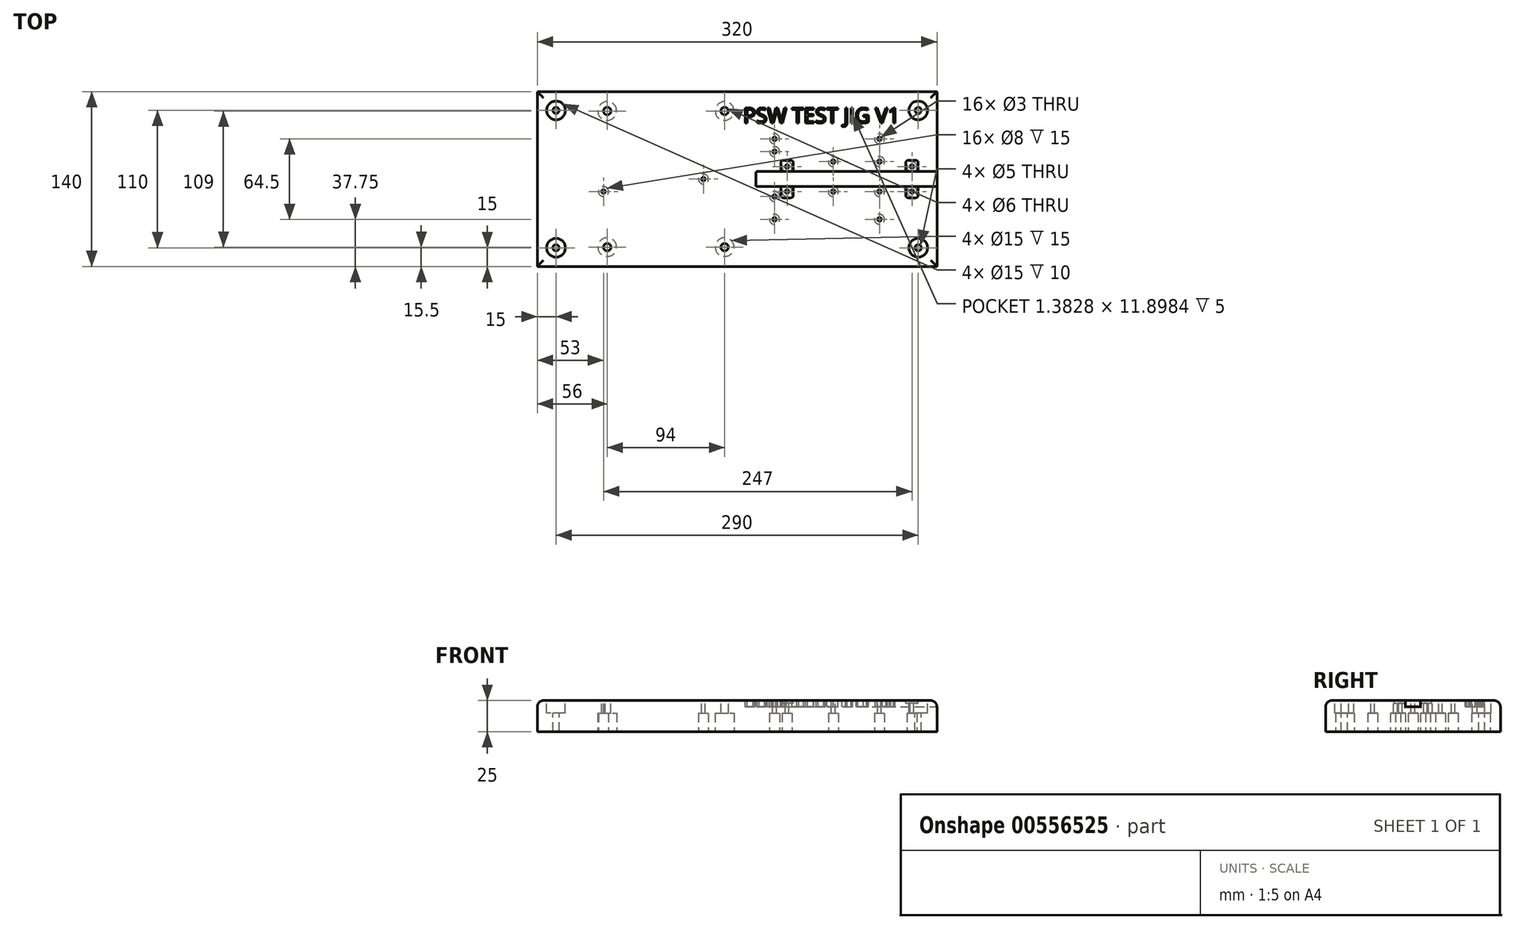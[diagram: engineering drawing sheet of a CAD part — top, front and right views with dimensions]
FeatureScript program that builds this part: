
annotation { "Feature Type Name" : "Feature", "Feature Type Description" : "" }
export const myFeature = defineFeature(function(context is Context, id is Id, definition is map)
    precondition{}
    {
        {
            var Q0;
            Q0=qCreatedBy(makeId("Top.planeOp"),FACE);
            var sketch = newSketch(context, id + "F0", { "sketchPlane" : qUnion([Q0])});
            skLineSegment(sketch, "E0.bottom", {"start": v(160, -70) * mm, "end": v(-160, -70) * mm});
            skLineSegment(sketch, "E0.top", {"start": v(160, 70) * mm, "end": v(-160, 70) * mm});
            skLineSegment(sketch, "E0.left", {"start": v(160, -70) * mm, "end": v(160, 70) * mm});
            skLineSegment(sketch, "E0.right", {"start": v(-160, -70) * mm, "end": v(-160, 70) * mm});
            skPoint(sketch, "E0.middle", {"position": v(0, 0) * mm});
            skSolve(sketch);
        }
        {
            var Q0;
            Q0 = qSketchRegion(id + "F0", true);
            extrude(context, id + "F1", {"entities" : qUnion([Q0]), "depth" : 25 * mm, "offsetDistance" : 25 * mm});
        }
        {
            var Q0;
            Q0=makeQuery(id+"F1.opExtrude","CAP_EDGE",EDGE,{"disambiguationData":[OSD([sQuery(id+"F0.wireOp",EDGE,"E0.right")])],"isStart":false});
            var Q1;
            Q1=makeQuery(id+"F1.opExtrude","CAP_EDGE",EDGE,{"disambiguationData":[OSD([sQuery(id+"F0.wireOp",EDGE,"E0.top")])],"isStart":false});
            var Q2;
            Q2=makeQuery(id+"F1.opExtrude","CAP_EDGE",EDGE,{"disambiguationData":[OSD([sQuery(id+"F0.wireOp",EDGE,"E0.left")])],"isStart":false});
            var Q3;
            Q3=makeQuery(id+"F1.opExtrude","CAP_EDGE",EDGE,{"disambiguationData":[OSD([sQuery(id+"F0.wireOp",EDGE,"E0.bottom")])],"isStart":false});
            fillet(context, id + "F2", {"entities" : qUnion([Q0, Q1, Q2, Q3]), "radius" : 5 * mm, "tangentPropagation" : true, "allowEdgeOverflow" : false});
        }
        {
            var Q0;
            Q0=makeQuery(id+"F1.opExtrude","CAP_FACE",FACE,{"disambiguationData":[OSD([sQuery(id+"F0.wireOp",EDGE,"E0.bottom"),sQuery(id+"F0.wireOp",EDGE,"E0.top"),sQuery(id+"F0.wireOp",EDGE,"E0.left"),sQuery(id+"F0.wireOp",EDGE,"E0.right")])],"isStart":false});
            var sketch = newSketch(context, id + "F3", { "sketchPlane" : qUnion([Q0])});
            skLineSegment(sketch, "E1", {"start": v(-346.3, 45) * mm, "end": v(340.15, 45) * mm, "construction": true});
            skText(sketch, "E2", { "text": "PSW TEST JIG V1", "fontName": "OpenSans-Regular.ttf"});
            const initialGuessF3  = {"E2": [0.005, 0.045, 1, 0, 0.012]};
            skSetInitialGuess(sketch, initialGuessF3);
            skSolve(sketch);
        }
        {
            var Q0;
            Q0 = qSketchRegion(id + "F3", true);
            extrude(context, id + "F4", {"entities" : qUnion([Q0]), "operationType" : NewBodyOperationType.REMOVE, "oppositeDirection" : true, "depth" : 5 * mm, "offsetDistance" : 25 * mm});
        }
        {
            var Q0;
            Q0=makeQuery(id+"F1.opExtrude","CAP_FACE",FACE,{"disambiguationData":[OSD([sQuery(id+"F0.wireOp",EDGE,"E0.bottom"),sQuery(id+"F0.wireOp",EDGE,"E0.top"),sQuery(id+"F0.wireOp",EDGE,"E0.left"),sQuery(id+"F0.wireOp",EDGE,"E0.right")])],"isStart":false});
            var sketch = newSketch(context, id + "F5", { "sketchPlane" : qUnion([Q0])});
            skCircle(sketch, "E3", {"center": v(-104, 54.5) * mm, "radius": 3 * mm});
            skLineSegment(sketch, "E4", {"start": v(-173, 0) * mm, "end": v(190.46, 0) * mm, "construction": true});
            skPoint(sketch, "E4.startSnap0", {"position": v(-155, 0) * mm});
            skCircle(sketch, "E5", {"center": v(-10, 54.5) * mm, "radius": 3 * mm});
            skLineSegment(sketch, "E6", {"start": v(0, 91.65) * mm, "end": v(0, -104.84) * mm, "construction": true});
            skCircle(sketch, "E7.MirrorC", {"center": v(-104, -54.5) * mm, "radius": 3 * mm});
            skCircle(sketch, "E8.MirrorC", {"center": v(-10, -54.5) * mm, "radius": 3 * mm});
            skCircle(sketch, "E9", {"center": v(-27, 0) * mm, "radius": 1.5 * mm});
            skCircle(sketch, "E10", {"center": v(-107, -10) * mm, "radius": 1.5 * mm});
            skSolve(sketch);
        }
        {
            var Q0;
            Q0 = qSketchRegion(id + "F5", true);
            extrude(context, id + "F6", {"entities" : qUnion([Q0]), "operationType" : NewBodyOperationType.REMOVE, "oppositeDirection" : true, "depth" : 25 * mm, "offsetDistance" : 25 * mm});
        }
        {
            var Q0;
            Q0=makeQuery(id+"F1.opExtrude","CAP_FACE",FACE,{"disambiguationData":[OSD([sQuery(id+"F0.wireOp",EDGE,"E0.bottom"),sQuery(id+"F0.wireOp",EDGE,"E0.top"),sQuery(id+"F0.wireOp",EDGE,"E0.left"),sQuery(id+"F0.wireOp",EDGE,"E0.right")])],"isStart":true});
            var sketch = newSketch(context, id + "F7", { "sketchPlane" : qUnion([Q0])});
            skCircle(sketch, "E11", {"center": v(-104, 54.5) * mm, "radius": 7.5 * mm});
            skCircle(sketch, "E12", {"center": v(-10, 54.5) * mm, "radius": 7.5 * mm});
            skCircle(sketch, "E13", {"center": v(-10, -54.5) * mm, "radius": 7.5 * mm});
            skCircle(sketch, "E14", {"center": v(-104, -54.5) * mm, "radius": 7.5 * mm});
            skCircle(sketch, "E15", {"center": v(-107, 10) * mm, "radius": 4 * mm});
            skCircle(sketch, "E16", {"center": v(-27, 0) * mm, "radius": 4 * mm});
            skSolve(sketch);
        }
        {
            var Q0;
            Q0 = qSketchRegion(id + "F7", true);
            extrude(context, id + "F8", {"entities" : qUnion([Q0]), "operationType" : NewBodyOperationType.REMOVE, "oppositeDirection" : true, "depth" : 15 * mm, "offsetDistance" : 25 * mm});
        }
        {
            var Q0;
            Q0=makeQuery(id+"F1.opExtrude","CAP_FACE",FACE,{"disambiguationData":[OSD([sQuery(id+"F0.wireOp",EDGE,"E0.bottom"),sQuery(id+"F0.wireOp",EDGE,"E0.top"),sQuery(id+"F0.wireOp",EDGE,"E0.left"),sQuery(id+"F0.wireOp",EDGE,"E0.right")])],"isStart":false});
            var sketch = newSketch(context, id + "F9", { "sketchPlane" : qUnion([Q0])});
            skLineSegment(sketch, "E17", {"start": v(-172.65, 0) * mm, "end": v(214.17, 0) * mm, "construction": true});
            skLineSegment(sketch, "E18", {"start": v(0, 95.62) * mm, "end": v(0, -102.66) * mm, "construction": true});
            skCircle(sketch, "E19", {"center": v(30, 32.25) * mm, "radius": 1.5 * mm});
            skCircle(sketch, "E20", {"center": v(114, 32.25) * mm, "radius": 1.5 * mm});
            skCircle(sketch, "E21.MirrorC", {"center": v(30, -32.25) * mm, "radius": 1.5 * mm});
            skCircle(sketch, "E22.MirrorC", {"center": v(114, -32.25) * mm, "radius": 1.5 * mm});
            skSolve(sketch);
        }
        {
            var Q0;
            Q0 = qSketchRegion(id + "F9", true);
            extrude(context, id + "F10", {"entities" : qUnion([Q0]), "operationType" : NewBodyOperationType.REMOVE, "oppositeDirection" : true, "depth" : 25 * mm, "offsetDistance" : 25 * mm});
        }
        {
            var Q0;
            Q0=makeQuery(id+"F1.opExtrude","CAP_FACE",FACE,{"disambiguationData":[OSD([sQuery(id+"F0.wireOp",EDGE,"E0.bottom"),sQuery(id+"F0.wireOp",EDGE,"E0.top"),sQuery(id+"F0.wireOp",EDGE,"E0.left"),sQuery(id+"F0.wireOp",EDGE,"E0.right")])],"isStart":true});
            var sketch = newSketch(context, id + "F11", { "sketchPlane" : qUnion([Q0])});
            skCircle(sketch, "E23", {"center": v(30, 32.25) * mm, "radius": 4 * mm});
            skCircle(sketch, "E24", {"center": v(114, 32.25) * mm, "radius": 4 * mm});
            skCircle(sketch, "E25", {"center": v(114, -32.25) * mm, "radius": 4 * mm});
            skCircle(sketch, "E26", {"center": v(30, -32.25) * mm, "radius": 4 * mm});
            skSolve(sketch);
        }
        {
            var Q0;
            Q0 = qSketchRegion(id + "F11", true);
            extrude(context, id + "F12", {"entities" : qUnion([Q0]), "operationType" : NewBodyOperationType.REMOVE, "oppositeDirection" : true, "depth" : 15 * mm, "offsetDistance" : 25 * mm});
        }
        {
            var Q0;
            Q0=makeQuery(id+"F1.opExtrude","CAP_FACE",FACE,{"disambiguationData":[OSD([sQuery(id+"F0.wireOp",EDGE,"E0.bottom"),sQuery(id+"F0.wireOp",EDGE,"E0.top"),sQuery(id+"F0.wireOp",EDGE,"E0.left"),sQuery(id+"F0.wireOp",EDGE,"E0.right")])],"isStart":false});
            var sketch = newSketch(context, id + "F13", { "sketchPlane" : qUnion([Q0])});
            skLineSegment(sketch, "E27", {"start": v(-174.59, 0) * mm, "end": v(211.52, 0) * mm, "construction": true});
            skLineSegment(sketch, "E28", {"start": v(0, 99.62) * mm, "end": v(0, -109.76) * mm, "construction": true});
            skCircle(sketch, "E29", {"center": v(-145, 55) * mm, "radius": 2.5 * mm});
            skCircle(sketch, "E30.MirrorC", {"center": v(-145, -55) * mm, "radius": 2.5 * mm});
            skLineSegment(sketch, "E31.MirrorCS", {"start": v(0, -99.62) * mm, "end": v(0, 109.76) * mm, "construction": true});
            skCircle(sketch, "E32.MirrorC", {"center": v(145, 55) * mm, "radius": 2.5 * mm});
            skCircle(sketch, "E33.MirrorC", {"center": v(145, -55) * mm, "radius": 2.5 * mm});
            skSolve(sketch);
        }
        {
            var Q0;
            Q0 = qSketchRegion(id + "F13", true);
            extrude(context, id + "F14", {"entities" : qUnion([Q0]), "operationType" : NewBodyOperationType.REMOVE, "oppositeDirection" : true, "depth" : 25 * mm, "offsetDistance" : 25 * mm});
        }
        {
            var Q0;
            Q0=makeQuery(id+"F1.opExtrude","CAP_FACE",FACE,{"disambiguationData":[OSD([sQuery(id+"F0.wireOp",EDGE,"E0.bottom"),sQuery(id+"F0.wireOp",EDGE,"E0.top"),sQuery(id+"F0.wireOp",EDGE,"E0.left"),sQuery(id+"F0.wireOp",EDGE,"E0.right")])],"isStart":false});
            var sketch = newSketch(context, id + "F15", { "sketchPlane" : qUnion([Q0])});
            skCircle(sketch, "E34", {"center": v(-145, 55) * mm, "radius": 7.5 * mm});
            skCircle(sketch, "E35", {"center": v(-145, -55) * mm, "radius": 7.5 * mm});
            skCircle(sketch, "E36", {"center": v(145, -55) * mm, "radius": 7.5 * mm});
            skCircle(sketch, "E37", {"center": v(145, 55) * mm, "radius": 7.5 * mm});
            skSolve(sketch);
        }
        {
            var Q0;
            Q0 = qSketchRegion(id + "F15", true);
            extrude(context, id + "F16", {"entities" : qUnion([Q0]), "operationType" : NewBodyOperationType.REMOVE, "oppositeDirection" : true, "depth" : 10 * mm, "offsetDistance" : 25 * mm});
        }
        {
            var Q0;
            {var subQ0=sQuery(id+"F0.wireOp",EDGE,"E0.right");var subQ1=sQuery(id+"F0.wireOp",EDGE,"E0.left");var subQ2=sQuery(id+"F0.wireOp",EDGE,"E0.top");var subQ3=sQuery(id+"F0.wireOp",EDGE,"E0.bottom");Q0=makeQuery(id+"F4.boolean.opBoolean","SPLIT",FACE,{"disambiguationData":[TD([makeQuery(id+"F2.opFillet","BLEND_FACE",FACE,{"disambiguationData":[OSD([subQ3])]})])],"derivedFrom":makeQuery(id+"F1.opExtrude","CAP_FACE",FACE,{"disambiguationData":[OSD([subQ3,subQ2,subQ1,subQ0])],"isStart":false})});}
            var sketch = newSketch(context, id + "F17", { "sketchPlane" : qUnion([Q0])});
            skLineSegment(sketch, "E38", {"start": v(-182.2, 0) * mm, "end": v(196.75, 0) * mm, "construction": true});
            skPoint(sketch, "E38.startSnap0", {"position": v(-155, 0) * mm});
            skCircle(sketch, "E39", {"center": v(114, 14) * mm, "radius": 1.5 * mm});
            skCircle(sketch, "E40", {"center": v(77, 14) * mm, "radius": 1.5 * mm});
            skCircle(sketch, "E41", {"center": v(30, 22) * mm, "radius": 1.5 * mm});
            skCircle(sketch, "E42", {"center": v(30, -14) * mm, "radius": 1.5 * mm});
            skCircle(sketch, "E43", {"center": v(77, -10) * mm, "radius": 1.5 * mm});
            skCircle(sketch, "E44", {"center": v(114, -10) * mm, "radius": 1.5 * mm});
            skLineSegment(sketch, "E45", {"start": v(30, 32.25) * mm, "end": v(30, -32.25) * mm, "construction": true});
            skSolve(sketch);
        }
        {
            var Q0;
            Q0 = qSketchRegion(id + "F17", true);
            extrude(context, id + "F18", {"entities" : qUnion([Q0]), "operationType" : NewBodyOperationType.REMOVE, "oppositeDirection" : true, "depth" : 25 * mm, "offsetDistance" : 25 * mm});
        }
        {
            var Q0;
            Q0=makeQuery(id+"F1.opExtrude","CAP_FACE",FACE,{"disambiguationData":[OSD([sQuery(id+"F0.wireOp",EDGE,"E0.bottom"),sQuery(id+"F0.wireOp",EDGE,"E0.top"),sQuery(id+"F0.wireOp",EDGE,"E0.left"),sQuery(id+"F0.wireOp",EDGE,"E0.right")])],"isStart":true});
            var sketch = newSketch(context, id + "F19", { "sketchPlane" : qUnion([Q0])});
            skCircle(sketch, "E46", {"center": v(30, 14) * mm, "radius": 4 * mm});
            skCircle(sketch, "E47", {"center": v(77, 10) * mm, "radius": 4 * mm});
            skCircle(sketch, "E48", {"center": v(114, 10) * mm, "radius": 4 * mm});
            skCircle(sketch, "E49", {"center": v(114, -14) * mm, "radius": 4 * mm});
            skCircle(sketch, "E50", {"center": v(77, -14) * mm, "radius": 4 * mm});
            skCircle(sketch, "E51", {"center": v(30, -22) * mm, "radius": 4 * mm});
            skSolve(sketch);
        }
        {
            var Q0;
            Q0 = qSketchRegion(id + "F19", true);
            extrude(context, id + "F20", {"entities" : qUnion([Q0]), "operationType" : NewBodyOperationType.REMOVE, "oppositeDirection" : true, "depth" : 15 * mm, "offsetDistance" : 25 * mm});
        }
        {
            var Q0;
            {var subQ0=sQuery(id+"F0.wireOp",EDGE,"E0.right");var subQ1=sQuery(id+"F0.wireOp",EDGE,"E0.left");var subQ2=sQuery(id+"F0.wireOp",EDGE,"E0.top");var subQ3=sQuery(id+"F0.wireOp",EDGE,"E0.bottom");Q0=makeQuery(id+"F4.boolean.opBoolean","SPLIT",FACE,{"disambiguationData":[TD([makeQuery(id+"F2.opFillet","BLEND_FACE",FACE,{"disambiguationData":[OSD([subQ3])]})])],"derivedFrom":makeQuery(id+"F1.opExtrude","CAP_FACE",FACE,{"disambiguationData":[OSD([subQ3,subQ2,subQ1,subQ0])],"isStart":false})});}
            var sketch = newSketch(context, id + "F21", { "sketchPlane" : qUnion([Q0])});
            skLineSegment(sketch, "E52.bottom", {"start": v(15, -6) * mm, "end": v(160, -6) * mm});
            skLineSegment(sketch, "E52.top", {"start": v(15, 6) * mm, "end": v(160, 6) * mm});
            skLineSegment(sketch, "E52.left", {"start": v(15, -6) * mm, "end": v(15, 6) * mm});
            skLineSegment(sketch, "E52.right", {"start": v(160, -6) * mm, "end": v(160, 6) * mm});
            skSolve(sketch);
        }
        {
            var Q0;
            Q0 = qSketchRegion(id + "F21", true);
            extrude(context, id + "F22", {"entities" : qUnion([Q0]), "operationType" : NewBodyOperationType.REMOVE, "oppositeDirection" : true, "depth" : 5 * mm, "offsetDistance" : 25 * mm});
        }
        {
            var Q0;
            Q0=makeQuery(id+"F22.boolean.opBoolean","COPY",EDGE,{"derivedFrom":makeQuery(id+"F22.opExtrude","CAP_EDGE",EDGE,{"disambiguationData":[OSD([sQuery(id+"F21.wireOp",EDGE,"E52.left")])],"isStart":true})});
            var Q1;
            Q1=makeQuery(id+"F22.boolean.opBoolean","COPY",EDGE,{"derivedFrom":makeQuery(id+"F22.opExtrude","SWEPT_EDGE",EDGE,{"disambiguationData":[OSD([sQuery(id+"F21.wireOp",EDGE,"E52.top"),sQuery(id+"F21.wireOp",EDGE,"E52.left")])]})});
            var Q2;
            Q2=makeQuery(id+"F22.boolean.opBoolean","COPY",EDGE,{"derivedFrom":makeQuery(id+"F22.opExtrude","SWEPT_EDGE",EDGE,{"disambiguationData":[OSD([sQuery(id+"F21.wireOp",EDGE,"E52.bottom"),sQuery(id+"F21.wireOp",EDGE,"E52.left")])]})});
            var Q3;
            Q3=makeQuery(id+"F22.boolean.opBoolean","COPY",EDGE,{"derivedFrom":makeQuery(id+"F22.opExtrude","CAP_EDGE",EDGE,{"disambiguationData":[OSD([sQuery(id+"F21.wireOp",EDGE,"E52.right")])],"isStart":false})});
            var Q4;
            {var subQ0=sQuery(id+"F0.wireOp",EDGE,"E0.left");Q4=makeQuery(id+"F22.boolean.opBoolean","MERGE",EDGE,{"derivedFrom":[makeQuery(id+"F2.opFillet","BLEND_EDGE",EDGE,{"blendedFrom":[makeQuery(id+"F1.opExtrude","CAP_EDGE",EDGE,{"disambiguationData":[OSD([subQ0])],"isStart":false}),makeQuery(id+"F1.opExtrude","SWEPT_FACE",FACE,{"disambiguationData":[OSD([subQ0])]})],"blendedInto":[makeQuery(id+"F1.opExtrude","SWEPT_FACE",FACE,{"disambiguationData":[OSD([subQ0])]})]}),makeQuery(id+"F22.opExtrude","CAP_EDGE",EDGE,{"disambiguationData":[OSD([sQuery(id+"F21.wireOp",EDGE,"E52.right")])],"isStart":false})]});}
            fillet(context, id + "F23", {"entities" : qUnion([Q0, Q1, Q2, Q3, Q4]), "radius" : 1 * mm, "tangentPropagation" : true, "allowEdgeOverflow" : false});
        }
        {
            var Q0;
            {var subQ0=sQuery(id+"F0.wireOp",EDGE,"E0.right");var subQ1=sQuery(id+"F0.wireOp",EDGE,"E0.left");var subQ2=sQuery(id+"F0.wireOp",EDGE,"E0.top");var subQ3=sQuery(id+"F0.wireOp",EDGE,"E0.bottom");Q0=makeQuery(id+"F4.boolean.opBoolean","SPLIT",FACE,{"disambiguationData":[TD([makeQuery(id+"F2.opFillet","BLEND_FACE",FACE,{"disambiguationData":[OSD([subQ3])]})])],"derivedFrom":makeQuery(id+"F1.opExtrude","CAP_FACE",FACE,{"disambiguationData":[OSD([subQ3,subQ2,subQ1,subQ0])],"isStart":false})});}
            var sketch = newSketch(context, id + "F24", { "sketchPlane" : qUnion([Q0])});
            skLineSegment(sketch, "E53", {"start": v(-16.3, 0) * mm, "end": v(165.04, 0) * mm, "construction": true});
            skLineSegment(sketch, "E54.bottom", {"start": v(45, -15) * mm, "end": v(35, -15) * mm});
            skLineSegment(sketch, "E54.top", {"start": v(45, 15) * mm, "end": v(35, 15) * mm});
            skLineSegment(sketch, "E54.left", {"start": v(45, -15) * mm, "end": v(45, 15) * mm});
            skLineSegment(sketch, "E54.right", {"start": v(35, -15) * mm, "end": v(35, 15) * mm});
            skPoint(sketch, "E54.middle", {"position": v(40, 0) * mm});
            skLineSegment(sketch, "E55.bottom", {"start": v(145, -15) * mm, "end": v(135, -15) * mm});
            skLineSegment(sketch, "E55.top", {"start": v(145, 15) * mm, "end": v(135, 15) * mm});
            skLineSegment(sketch, "E55.left", {"start": v(145, -15) * mm, "end": v(145, 15) * mm});
            skLineSegment(sketch, "E55.right", {"start": v(135, -15) * mm, "end": v(135, 15) * mm});
            skPoint(sketch, "E55.middle", {"position": v(140, 0) * mm});
            skLineSegment(sketch, "E56", {"start": v(0, 78.47) * mm, "end": v(0, -93.79) * mm, "construction": true});
            skSolve(sketch);
        }
        {
            var Q0;
            Q0 = qSketchRegion(id + "F24", true);
            extrude(context, id + "F25", {"entities" : qUnion([Q0]), "operationType" : NewBodyOperationType.REMOVE, "oppositeDirection" : true, "depth" : 2 * mm, "offsetDistance" : 25 * mm});
        }
        {
            var Q0;
            Q0=makeQuery(id+"F25.boolean.opBoolean","COPY",EDGE,{"derivedFrom":makeQuery(id+"F25.opExtrude","SWEPT_EDGE",EDGE,{"disambiguationData":[OSD([sQuery(id+"F24.wireOp",EDGE,"E54.top"),sQuery(id+"F24.wireOp",EDGE,"E54.right")])]})});
            var Q1;
            Q1=makeQuery(id+"F25.boolean.opBoolean","COPY",EDGE,{"derivedFrom":makeQuery(id+"F25.opExtrude","SWEPT_EDGE",EDGE,{"disambiguationData":[OSD([sQuery(id+"F24.wireOp",EDGE,"E54.top"),sQuery(id+"F24.wireOp",EDGE,"E54.left")])]})});
            var Q2;
            Q2=makeQuery(id+"F25.boolean.opBoolean","COPY",EDGE,{"derivedFrom":makeQuery(id+"F25.opExtrude","SWEPT_EDGE",EDGE,{"disambiguationData":[OSD([sQuery(id+"F24.wireOp",EDGE,"E54.bottom"),sQuery(id+"F24.wireOp",EDGE,"E54.right")])]})});
            var Q3;
            Q3=makeQuery(id+"F25.boolean.opBoolean","COPY",EDGE,{"derivedFrom":makeQuery(id+"F25.opExtrude","SWEPT_EDGE",EDGE,{"disambiguationData":[OSD([sQuery(id+"F24.wireOp",EDGE,"E54.bottom"),sQuery(id+"F24.wireOp",EDGE,"E54.left")])]})});
            var Q4;
            Q4=makeQuery(id+"F25.boolean.opBoolean","COPY",EDGE,{"derivedFrom":makeQuery(id+"F25.opExtrude","SWEPT_EDGE",EDGE,{"disambiguationData":[OSD([sQuery(id+"F24.wireOp",EDGE,"E55.top"),sQuery(id+"F24.wireOp",EDGE,"E55.right")])]})});
            var Q5;
            Q5=makeQuery(id+"F25.boolean.opBoolean","COPY",EDGE,{"derivedFrom":makeQuery(id+"F25.opExtrude","SWEPT_EDGE",EDGE,{"disambiguationData":[OSD([sQuery(id+"F24.wireOp",EDGE,"E55.top"),sQuery(id+"F24.wireOp",EDGE,"E55.left")])]})});
            var Q6;
            Q6=makeQuery(id+"F25.boolean.opBoolean","COPY",EDGE,{"derivedFrom":makeQuery(id+"F25.opExtrude","SWEPT_EDGE",EDGE,{"disambiguationData":[OSD([sQuery(id+"F24.wireOp",EDGE,"E55.bottom"),sQuery(id+"F24.wireOp",EDGE,"E55.right")])]})});
            var Q7;
            Q7=makeQuery(id+"F25.boolean.opBoolean","COPY",EDGE,{"derivedFrom":makeQuery(id+"F25.opExtrude","SWEPT_EDGE",EDGE,{"disambiguationData":[OSD([sQuery(id+"F24.wireOp",EDGE,"E55.bottom"),sQuery(id+"F24.wireOp",EDGE,"E55.left")])]})});
            fillet(context, id + "F26", {"entities" : qUnion([Q0, Q1, Q2, Q3, Q4, Q5, Q6, Q7]), "radius" : 2 * mm, "tangentPropagation" : true, "allowEdgeOverflow" : false});
        }
        {
            var Q0;
            {var subQ0=sQuery(id+"F0.wireOp",EDGE,"E0.right");var subQ1=sQuery(id+"F0.wireOp",EDGE,"E0.left");var subQ2=sQuery(id+"F0.wireOp",EDGE,"E0.top");var subQ3=sQuery(id+"F0.wireOp",EDGE,"E0.bottom");Q0=makeQuery(id+"F4.boolean.opBoolean","SPLIT",FACE,{"disambiguationData":[TD([makeQuery(id+"F2.opFillet","BLEND_FACE",FACE,{"disambiguationData":[OSD([subQ3])]})])],"derivedFrom":makeQuery(id+"F1.opExtrude","CAP_FACE",FACE,{"disambiguationData":[OSD([subQ3,subQ2,subQ1,subQ0])],"isStart":false})});}
            var sketch = newSketch(context, id + "F27", { "sketchPlane" : qUnion([Q0])});
            skLineSegment(sketch, "E57", {"start": v(0, 0) * mm, "end": v(193.75, 0) * mm, "construction": true});
            skLineSegment(sketch, "E58", {"start": v(0, 81.91) * mm, "end": v(0, -80.5) * mm, "construction": true});
            skLineSegment(sketch, "E59", {"start": v(40, 15) * mm, "end": v(40, -15) * mm, "construction": true});
            skLineSegment(sketch, "E60", {"start": v(140, 15) * mm, "end": v(140, -15) * mm, "construction": true});
            skLineSegment(sketch, "E61", {"start": v(40, 10) * mm, "end": v(140, 10) * mm, "construction": true});
            skLineSegment(sketch, "E62", {"start": v(40, -10) * mm, "end": v(140, -10) * mm, "construction": true});
            skCircle(sketch, "E63", {"center": v(40, 10) * mm, "radius": 1.5 * mm});
            skCircle(sketch, "E64", {"center": v(140, 10) * mm, "radius": 1.5 * mm});
            skCircle(sketch, "E65", {"center": v(40, -10) * mm, "radius": 1.5 * mm});
            skCircle(sketch, "E66", {"center": v(140, -10) * mm, "radius": 1.5 * mm});
            skSolve(sketch);
        }
        {
            var Q0;
            Q0 = qSketchRegion(id + "F27", true);
            extrude(context, id + "F28", {"entities" : qUnion([Q0]), "operationType" : NewBodyOperationType.REMOVE, "oppositeDirection" : true, "depth" : 25 * mm, "offsetDistance" : 25 * mm});
        }
        {
            var Q0;
            Q0=makeQuery(id+"F1.opExtrude","CAP_FACE",FACE,{"disambiguationData":[OSD([sQuery(id+"F0.wireOp",EDGE,"E0.bottom"),sQuery(id+"F0.wireOp",EDGE,"E0.top"),sQuery(id+"F0.wireOp",EDGE,"E0.left"),sQuery(id+"F0.wireOp",EDGE,"E0.right")])],"isStart":true});
            var sketch = newSketch(context, id + "F29", { "sketchPlane" : qUnion([Q0])});
            skCircle(sketch, "E67", {"center": v(40, -10) * mm, "radius": 4 * mm});
            skCircle(sketch, "E68", {"center": v(40, 10) * mm, "radius": 4 * mm});
            skCircle(sketch, "E69", {"center": v(140, 10) * mm, "radius": 4 * mm});
            skCircle(sketch, "E70", {"center": v(140, -10) * mm, "radius": 4 * mm});
            skSolve(sketch);
        }
        {
            var Q0;
            Q0 = qSketchRegion(id + "F29", true);
            extrude(context, id + "F30", {"entities" : qUnion([Q0]), "operationType" : NewBodyOperationType.REMOVE, "oppositeDirection" : true, "depth" : 15 * mm, "offsetDistance" : 25 * mm});
        }
    });
